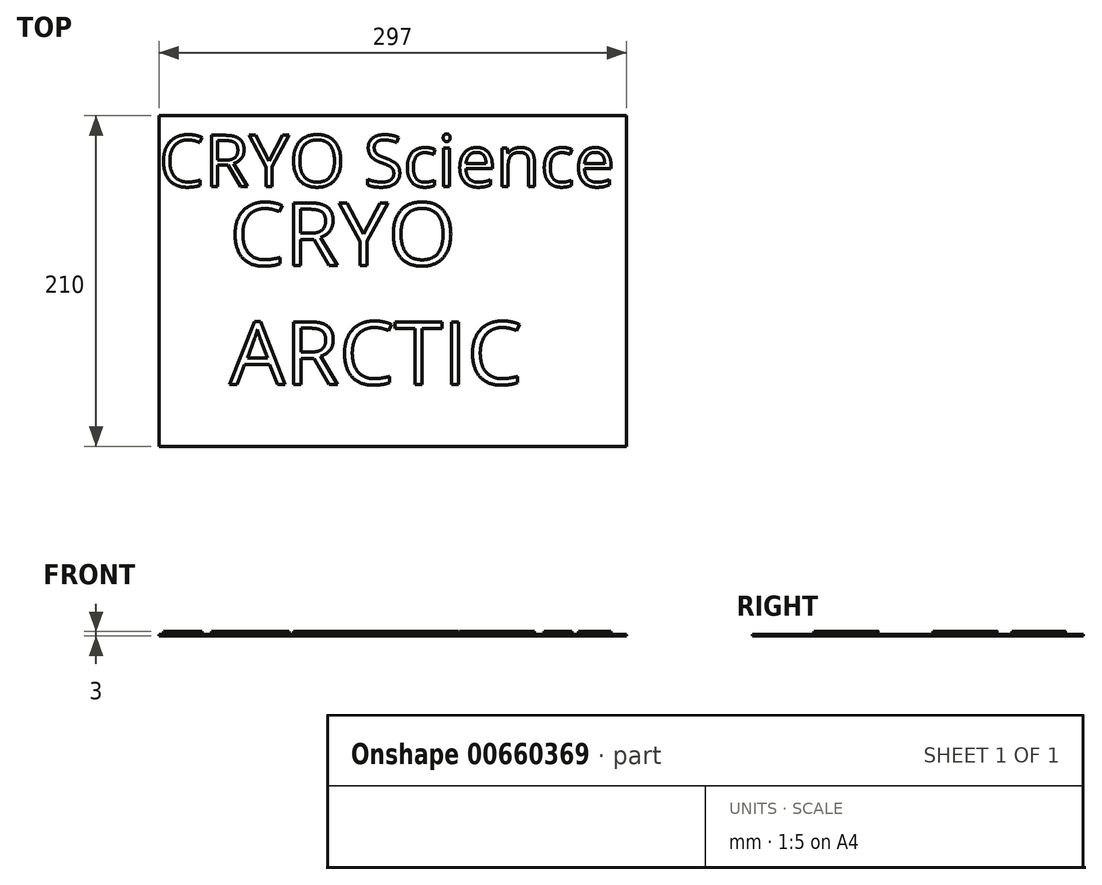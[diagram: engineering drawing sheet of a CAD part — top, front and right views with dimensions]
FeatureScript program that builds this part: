
annotation { "Feature Type Name" : "Feature", "Feature Type Description" : "" }
export const myFeature = defineFeature(function(context is Context, id is Id, definition is map)
    precondition{}
    {
        {
            var Q0;
            Q0=qCreatedBy(makeId("Top.planeOp"),FACE);
            var sketch = newSketch(context, id + "F0", { "sketchPlane" : qUnion([Q0])});
            skLineSegment(sketch, "E0.bottom", {"start": v(-84.03, 96.68) * mm, "end": v(212.97, 96.68) * mm});
            skLineSegment(sketch, "E0.top", {"start": v(-84.03, -113.32) * mm, "end": v(212.97, -113.32) * mm});
            skLineSegment(sketch, "E0.left", {"start": v(-84.03, 96.68) * mm, "end": v(-84.03, -113.32) * mm});
            skLineSegment(sketch, "E0.right", {"start": v(212.97, 96.68) * mm, "end": v(212.97, -113.32) * mm});
            skSolve(sketch);
        }
        {
            var Q0;
            Q0=qSketchRegion(id+"F0",true);
            extrude(context, id + "F1", {"entities" : qUnion([Q0]), "depth" : 1 * mm, "offsetDistance" : 25 * mm});
        }
        {
            var Q0;
            Q0=makeQuery(id+"F1.opExtrude","CAP_FACE",FACE,{"disambiguationData":[OSD([sQuery(id+"F0.wireOp",EDGE,"E0.bottom"),sQuery(id+"F0.wireOp",EDGE,"E0.top"),sQuery(id+"F0.wireOp",EDGE,"E0.left"),sQuery(id+"F0.wireOp",EDGE,"E0.right")])],"isStart":false});
            var sketch = newSketch(context, id + "F2", { "sketchPlane" : qUnion([Q0])});
            skText(sketch, "E1", { "text": "CRYO Science", "fontName": "OpenSans-Regular.ttf"});
            skText(sketch, "E2", { "text": "CRYO\nARCTIC", "fontName": "OpenSans-Regular.ttf"});
            const initialGuessF2  = {"E1": [-0.08403, 0.05168, 1, 0, 0.03288], "E2": [-0.03915, 0.00168, 1, 0, 0.04]};
            skSetInitialGuess(sketch, initialGuessF2);
            skSolve(sketch);
        }
        {
            var Q0;
            Q0=qSketchRegion(id+"F2",true);
            extrude(context, id + "F3", {"entities" : qUnion([Q0]), "operationType" : NewBodyOperationType.ADD, "depth" : 2 * mm, "offsetDistance" : 25 * mm});
        }
    });
